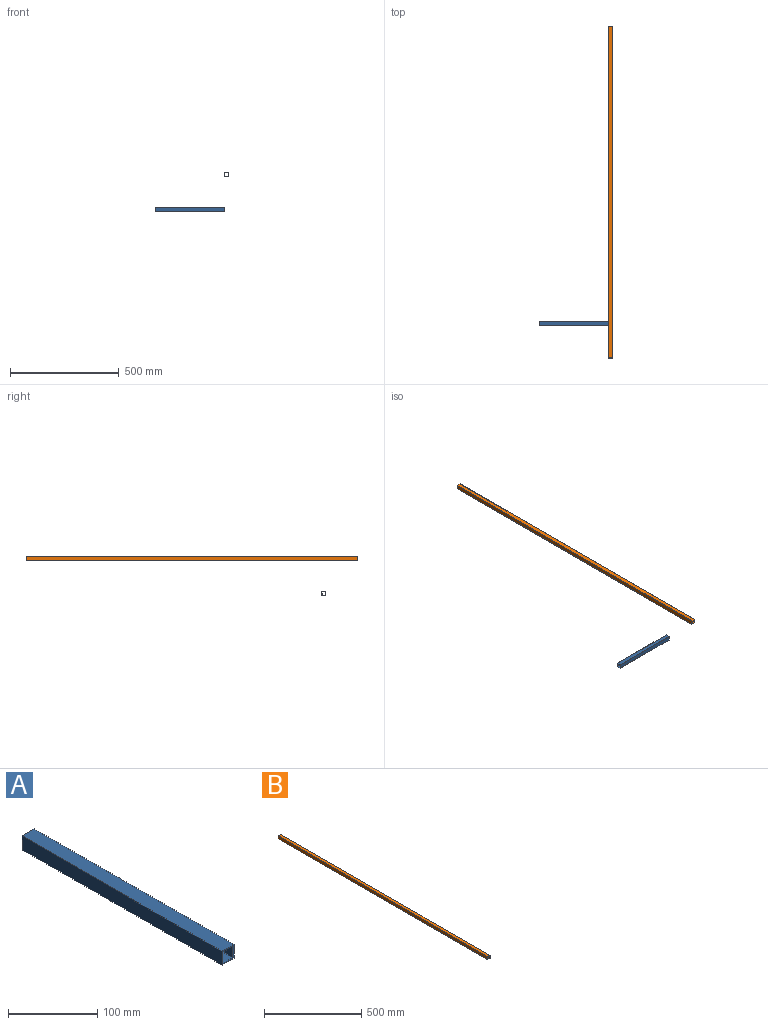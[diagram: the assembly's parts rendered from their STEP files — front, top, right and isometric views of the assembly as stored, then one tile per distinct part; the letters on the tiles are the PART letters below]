
ASSEMBLY  parts=2 mates=4
PART A: 10 faces, bbox 19.1x317.5x19.1 mm
  f0: plane 317.5x19.05mm, normal (0,0,1), area 6048.4mm2, adj f1,f7,f8,f9
  f1: plane 317.5x19.05mm, normal (-1,0,0), area 6048.4mm2, adj f0,f2,f8,f9
  f2: plane 317.5x19.05mm, normal (0,0,-1), area 6048.4mm2, adj f1,f7,f8,f9
  f3: plane 317.5x15.88mm, normal (1,0,0), area 5040.3mm2, adj f4,f6,f8,f9
  f4: plane 317.5x15.88mm, normal (0,0,-1), area 5040.3mm2, adj f3,f5,f8,f9
  f5: plane 317.5x15.88mm, normal (-1,0,0), area 5040.3mm2, adj f4,f6,f8,f9
  f6: plane 317.5x15.88mm, normal (0,0,1), area 5040.3mm2, adj f3,f5,f8,f9
  f7: plane 317.5x19.05mm, normal (1,0,0), area 6048.4mm2, adj f0,f2,f8,f9
  f8: plane 19.05x19.05mm, normal (0,-1,0), area 110.9mm2, adj f0,f1,f2,f3,f4,f5,f6,f7
  f9: plane 19.05x19.05mm, normal (0,1,0), area 110.9mm2, adj f0,f1,f2,f3,f4,f5,f6,f7
PART B: 10 faces, bbox 19.1x1524x19.1 mm
  f0: plane 1524x15.88mm, normal (0,0,-1), area 24193.5mm2, adj f1,f7,f8,f9
  f1: plane 1524x15.88mm, normal (-1,0,0), area 24193.5mm2, adj f0,f2,f8,f9
  f2: plane 1524x15.88mm, normal (0,0,1), area 24193.5mm2, adj f1,f7,f8,f9
  f3: plane 1524x19.05mm, normal (0,0,1), area 29032.2mm2, adj f4,f6,f8,f9
  f4: plane 1524x19.05mm, normal (-1,0,0), area 29032.2mm2, adj f3,f5,f8,f9
  f5: plane 1524x19.05mm, normal (0,0,-1), area 29032.2mm2, adj f4,f6,f8,f9
  f6: plane 1524x19.05mm, normal (1,0,0), area 29032.2mm2, adj f3,f5,f8,f9
  f7: plane 1524x15.88mm, normal (1,0,0), area 24193.5mm2, adj f0,f2,f8,f9
  f8: plane 19.05x19.05mm, normal (0,-1,0), area 110.9mm2, adj f0,f1,f2,f3,f4,f5,f6,f7
  f9: plane 19.05x19.05mm, normal (0,1,0), area 110.9mm2, adj f0,f1,f2,f3,f4,f5,f6,f7
PLACE A rot(axis=(-0.58,-0.58,-0.58),120deg) t=(936.24,-483.79,-60.95)mm
PLACE B t=(945.76,882.96,100.78)mm
MATE parallel A.f2 <-> B.f8  axis (0,-1,0) through (777.49,-493.31,-60.95)mm
MATE parallel A.f2 <-> B.f8  axis (0,-1,0) through (777.49,-493.31,-60.95)mm
MATE planar A.f9 <-> B.f4  axis (1,0,0) through (936.24,-475.85,-53.01)mm
MATE parallel A.f7 <-> B.f3  axis (0,0,1) through (777.49,-483.79,-51.43)mm
